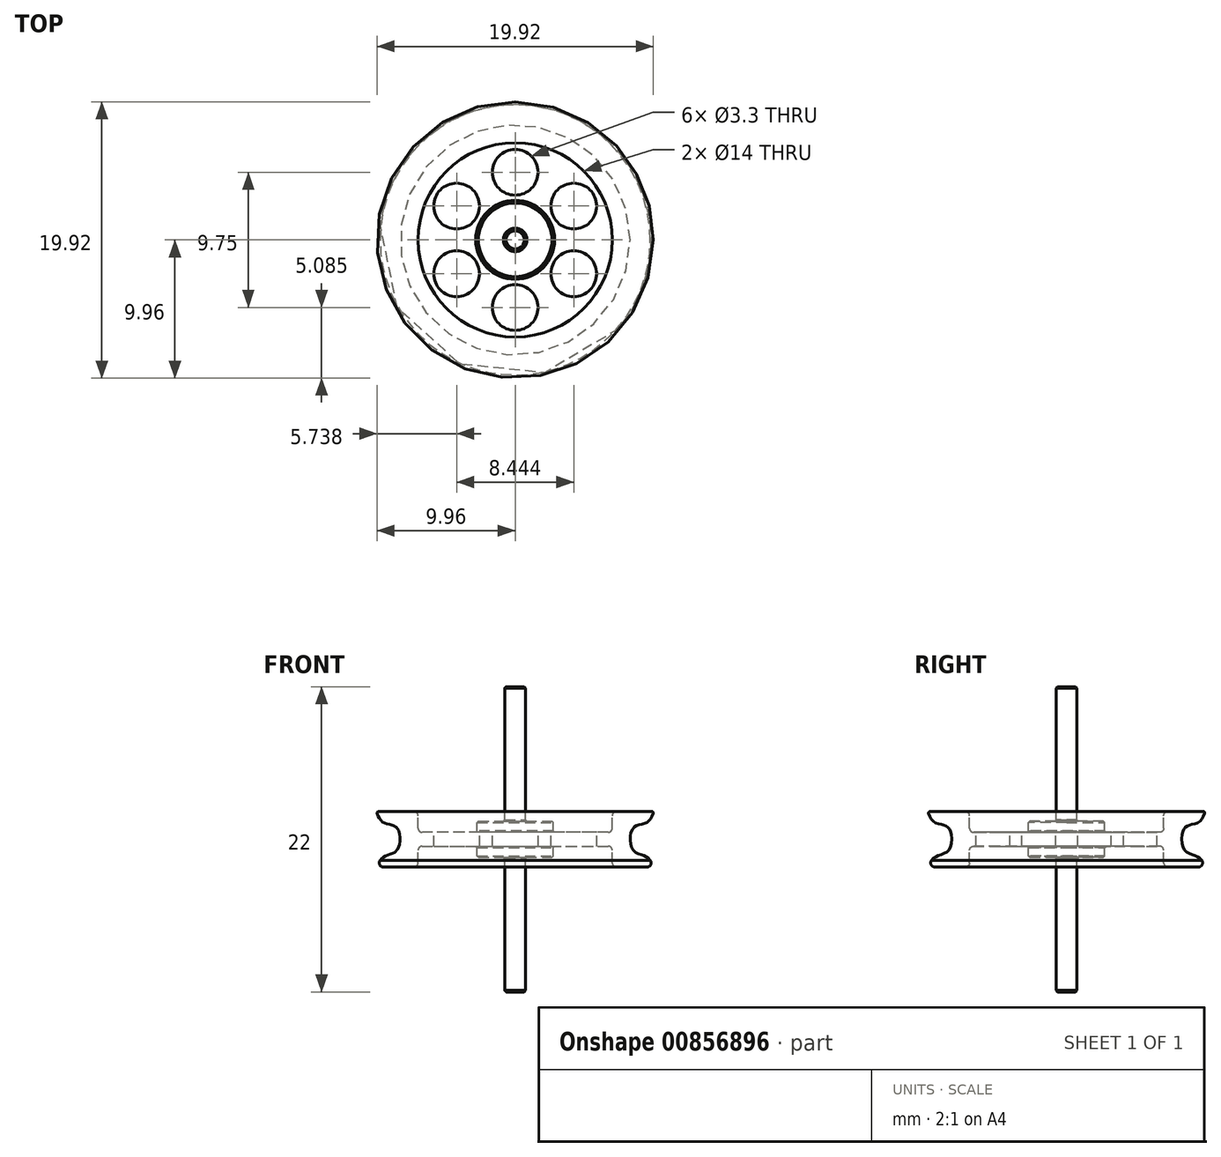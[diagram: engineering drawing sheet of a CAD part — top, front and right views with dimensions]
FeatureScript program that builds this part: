
annotation { "Feature Type Name" : "Feature", "Feature Type Description" : "" }
export const myFeature = defineFeature(function(context is Context, id is Id, definition is map)
    precondition{}
    {
        {
            var Q0;
            Q0=qCreatedBy(makeId("Front.planeOp"),FACE);
            var sketch = newSketch(context, id + "F0", { "sketchPlane" : qUnion([Q0])});
            skLineSegment(sketch, "E0", {"start": v(-2.75, 3.55) * mm, "end": v(-7, 3.55) * mm});
            skLineSegment(sketch, "E1", {"start": v(-7, 3.55) * mm, "end": v(-7, 5.05) * mm});
            skLineSegment(sketch, "E2", {"start": v(-7, 5.05) * mm, "end": v(-10, 5.05) * mm});
            skLineSegment(sketch, "E3", {"start": v(-10, 1.05) * mm, "end": v(-7, 1.05) * mm});
            skLineSegment(sketch, "E4", {"start": v(-7, 1.05) * mm, "end": v(-7, 2.55) * mm});
            skLineSegment(sketch, "E5", {"start": v(-7, 2.55) * mm, "end": v(-2.75, 2.55) * mm});
            skLineSegment(sketch, "E6", {"start": v(0, 2.55) * mm, "end": v(0, 3.55) * mm});
            skFitSpline(sketch, "E7", {"points": [v(-10, 5.05) * mm, v(-9.43, 4.22) * mm, v(-8.53, 3.89) * mm, v(-8.47, 2.33) * mm, v(-9.43, 1.8) * mm, v(-10, 1.05) * mm], "startDerivative": vector(2.2, -6.19) * mm, "endDerivative": vector(-2.16, -5.53) * mm});
            skLineSegment(sketch, "E8", {"start": v(-2.75, 3.55) * mm, "end": v(-2.75, 4.35) * mm});
            skLineSegment(sketch, "E9", {"start": v(-2.75, 4.35) * mm, "end": v(-0.75, 4.35) * mm});
            skLineSegment(sketch, "E10", {"start": v(-0.75, 4.35) * mm, "end": v(-0.75, 14.05) * mm});
            skLineSegment(sketch, "E11", {"start": v(-0.75, 14.05) * mm, "end": v(0, 14.05) * mm});
            skLineSegment(sketch, "E12", {"start": v(0, 14.05) * mm, "end": v(0, 3.55) * mm});
            skLineSegment(sketch, "E13", {"start": v(-13.06, 3.05) * mm, "end": v(7.06, 3.05) * mm, "construction": true});
            skLineSegment(sketch, "E14.MirrorCS", {"start": v(0, -7.95) * mm, "end": v(0, 2.55) * mm});
            skLineSegment(sketch, "E15.MirrorCS", {"start": v(0, 3.55) * mm, "end": v(0, 2.55) * mm});
            skLineSegment(sketch, "E16.MirrorCS", {"start": v(-2.75, 1.75) * mm, "end": v(-0.75, 1.75) * mm});
            skLineSegment(sketch, "E17.MirrorCS", {"start": v(-2.75, 2.55) * mm, "end": v(-2.75, 1.75) * mm});
            skLineSegment(sketch, "E18.MirrorCS", {"start": v(-0.75, 1.75) * mm, "end": v(-0.75, -7.95) * mm});
            skLineSegment(sketch, "E19.MirrorCS", {"start": v(-0.75, -7.95) * mm, "end": v(0, -7.95) * mm});
            skSolve(sketch);
        }
        {
            var Q0;
            Q0=makeQuery(id+"F0.imprint","IMPRINT",FACE,{"disambiguationData":[TD([[makeQuery(id+"F0.imprint","IMPRINT",EDGE,{"derivedFrom":sQuery(id+"F0.wireOp",EDGE,"E0")}),1.0]])]});
            var Q1;
            Q1=sQuery(id+"F0.wireOp",EDGE,"E15.MirrorCS");
            revolve(context, id + "F1", {"surfaceOperationType" : NewSurfaceOperationType.NEW, "entities" : qUnion([Q0]), "axis" : qUnion([Q1]), "revolveType" : RevolveType.FULL});
        }
        {
            var Q0;
            Q0=makeQuery(id+"F1.opRevolve","SWEPT_FACE",FACE,{"disambiguationData":[OSD([sQuery(id+"F0.wireOp",EDGE,"E0")])]});
            var sketch = newSketch(context, id + "F2", { "sketchPlane" : qUnion([Q0])});
            skCircle(sketch, "E20", {"center": v(0, 0) * mm, "radius": 4.88 * mm, "construction": true});
            skPoint(sketch, "E21.start.orphan", {"position": v(0, 2.75) * mm});
            skPoint(sketch, "E22", {"position": v(0, 4.88) * mm});
            skPoint(sketch, "E23.1.0", {"position": v(-4.22, -2.44) * mm});
            skPoint(sketch, "E23.2.0", {"position": v(4.22, -2.44) * mm});
            skCircle(sketch, "E24", {"center": v(-4.22, -2.44) * mm, "radius": 6 * mm, "construction": true});
            skCircle(sketch, "E25", {"center": v(0, 4.88) * mm, "radius": 6 * mm, "construction": true});
            skLineSegment(sketch, "E26", {"start": v(-5.8, 3.35) * mm, "end": v(1.58, -0.91) * mm, "construction": true});
            skPoint(sketch, "E27", {"position": v(-4.22, 2.44) * mm});
            skPoint(sketch, "E28.1.0", {"position": v(0, -4.87) * mm});
            skPoint(sketch, "E28.2.0", {"position": v(4.22, 2.44) * mm});
            skSolve(sketch);
        }
        {
            var Q0;
            Q0=sQuery(id+"F2.wireOp",VERTEX,"E22");
            var Q1;
            Q1=sQuery(id+"F2.wireOp",VERTEX,"E28.2.0");
            var Q2;
            Q2=sQuery(id+"F2.wireOp",VERTEX,"E23.2.0");
            var Q3;
            Q3=sQuery(id+"F2.wireOp",VERTEX,"E28.1.0");
            var Q4;
            Q4=sQuery(id+"F2.wireOp",VERTEX,"E23.1.0");
            var Q5;
            Q5=sQuery(id+"F2.wireOp",VERTEX,"E27");
            var Q6;
            Q6=makeQuery(id+"F1.opRevolve","SWEPT_BODY",BODY,{"disambiguationData":[OSD([sQuery(id+"F0.wireOp",EDGE,"E0"),sQuery(id+"F0.wireOp",EDGE,"E1"),sQuery(id+"F0.wireOp",EDGE,"E2"),sQuery(id+"F0.wireOp",EDGE,"E3"),sQuery(id+"F0.wireOp",EDGE,"E4"),sQuery(id+"F0.wireOp",EDGE,"E5"),sQuery(id+"F0.wireOp",EDGE,"E7"),sQuery(id+"F0.wireOp",EDGE,"E8"),sQuery(id+"F0.wireOp",EDGE,"E9"),sQuery(id+"F0.wireOp",EDGE,"E10"),sQuery(id+"F0.wireOp",EDGE,"E11"),sQuery(id+"F0.wireOp",EDGE,"E12"),sQuery(id+"F0.wireOp",EDGE,"E14.MirrorCS"),sQuery(id+"F0.wireOp",EDGE,"E15.MirrorCS"),sQuery(id+"F0.wireOp",EDGE,"E16.MirrorCS"),sQuery(id+"F0.wireOp",EDGE,"E17.MirrorCS"),sQuery(id+"F0.wireOp",EDGE,"E18.MirrorCS"),sQuery(id+"F0.wireOp",EDGE,"E19.MirrorCS")])]});
            hole(context, id + "F3", {"style" : HoleStyle.SIMPLE, "endStyle" : HoleEndStyle.THROUGH, "holeDiameter" : 3.3 * mm, "majorDiameter" : 5 * mm, "isTappedThrough" : true, "tappedDepth" : 12 * mm, "tapClearance" : 3, "locations" : qUnion([Q0, Q1, Q2, Q3, Q4, Q5]), "scope" : qUnion([Q6])});
        }
        {
            var Q0;
            Q0=makeQuery(id+"F1.opRevolve","SWEPT_EDGE",EDGE,{"disambiguationData":[OSD([sQuery(id+"F0.wireOp",EDGE,"E1"),sQuery(id+"F0.wireOp",EDGE,"E2")])]});
            var Q1;
            Q1=makeQuery(id+"F1.opRevolve","SWEPT_EDGE",EDGE,{"disambiguationData":[OSD([sQuery(id+"F0.wireOp",EDGE,"E0"),sQuery(id+"F0.wireOp",EDGE,"E1")])]});
            var Q2;
            Q2=makeQuery(id+"F1.opRevolve","SWEPT_EDGE",EDGE,{"disambiguationData":[OSD([sQuery(id+"F0.wireOp",EDGE,"E4"),sQuery(id+"F0.wireOp",EDGE,"E5")])]});
            var Q3;
            Q3=makeQuery(id+"F1.opRevolve","SWEPT_FACE",FACE,{"disambiguationData":[OSD([sQuery(id+"F0.wireOp",EDGE,"E3")])]});
            fillet(context, id + "F4", {"entities" : qUnion([Q0, Q1, Q2, Q3]), "radius" : 0.3 * mm, "tangentPropagation" : true, "allowEdgeOverflow" : false});
        }
        {
            var Q0;
            Q0=makeQuery(id+"F3.hole-1.boolean.opBoolean","COPY",FACE,{"derivedFrom":makeQuery(id+"F3.hole-1.opRevolve","SWEPT_FACE",FACE,{"disambiguationData":[OSD([sQuery(id+"F3.hole-1.sketch.wireOp",EDGE,"core_line_2")])]})});
            var Q1;
            Q1=makeQuery(id+"F3.hole-2.boolean.opBoolean","COPY",FACE,{"derivedFrom":makeQuery(id+"F3.hole-2.opRevolve","SWEPT_FACE",FACE,{"disambiguationData":[OSD([sQuery(id+"F3.hole-2.sketch.wireOp",EDGE,"core_line_2")])]})});
            var Q2;
            Q2=makeQuery(id+"F3.hole-3.boolean.opBoolean","COPY",FACE,{"derivedFrom":makeQuery(id+"F3.hole-3.opRevolve","SWEPT_FACE",FACE,{"disambiguationData":[OSD([sQuery(id+"F3.hole-3.sketch.wireOp",EDGE,"core_line_2")])]})});
            var Q3;
            Q3=makeQuery(id+"F3.hole-4.boolean.opBoolean","COPY",FACE,{"derivedFrom":makeQuery(id+"F3.hole-4.opRevolve","SWEPT_FACE",FACE,{"disambiguationData":[OSD([sQuery(id+"F3.hole-4.sketch.wireOp",EDGE,"core_line_2")])]})});
            var Q4;
            Q4=makeQuery(id+"F3.hole-5.boolean.opBoolean","COPY",FACE,{"derivedFrom":makeQuery(id+"F3.hole-5.opRevolve","SWEPT_FACE",FACE,{"disambiguationData":[OSD([sQuery(id+"F3.hole-5.sketch.wireOp",EDGE,"core_line_2")])]})});
            var Q5;
            Q5=makeQuery(id+"F3.hole-0.boolean.opBoolean","COPY",FACE,{"derivedFrom":makeQuery(id+"F3.hole-0.opRevolve","SWEPT_FACE",FACE,{"disambiguationData":[OSD([sQuery(id+"F3.hole-0.sketch.wireOp",EDGE,"core_line_2")])]})});
            var Q6;
            Q6=makeQuery(id+"F1.opRevolve","SWEPT_FACE",FACE,{"disambiguationData":[OSD([sQuery(id+"F0.wireOp",EDGE,"E8")])]});
            var Q7;
            Q7=makeQuery(id+"F1.opRevolve","SWEPT_EDGE",EDGE,{"disambiguationData":[OSD([sQuery(id+"F0.wireOp",EDGE,"E9"),sQuery(id+"F0.wireOp",EDGE,"E10")])]});
            var Q8;
            Q8=makeQuery(id+"F1.opRevolve","SWEPT_EDGE",EDGE,{"disambiguationData":[OSD([sQuery(id+"F0.wireOp",EDGE,"E10"),sQuery(id+"F0.wireOp",EDGE,"E11")])]});
            var Q9;
            Q9=makeQuery(id+"F1.opRevolve","SWEPT_FACE",FACE,{"disambiguationData":[OSD([sQuery(id+"F0.wireOp",EDGE,"E17.MirrorCS")])]});
            var Q10;
            Q10=makeQuery(id+"F1.opRevolve","SWEPT_FACE",FACE,{"disambiguationData":[OSD([sQuery(id+"F0.wireOp",EDGE,"E18.MirrorCS")])]});
            chamfer(context, id + "F5", {"entities" : qUnion([Q0, Q1, Q2, Q3, Q4, Q5, Q6, Q7, Q8, Q9, Q10]), "width" : 0.1 * mm, "tangentPropagation" : true});
        }
        {
            var Q0;
            Q0=makeQuery(id+"F1.opRevolve","SWEPT_EDGE",EDGE,{"disambiguationData":[OSD([sQuery(id+"F0.wireOp",EDGE,"E2"),sQuery(id+"F0.wireOp",EDGE,"E7")])]});
            fillet(context, id + "F6", {"entities" : qUnion([Q0]), "radius" : 0.1 * mm, "tangentPropagation" : true, "allowEdgeOverflow" : false});
        }
    });
